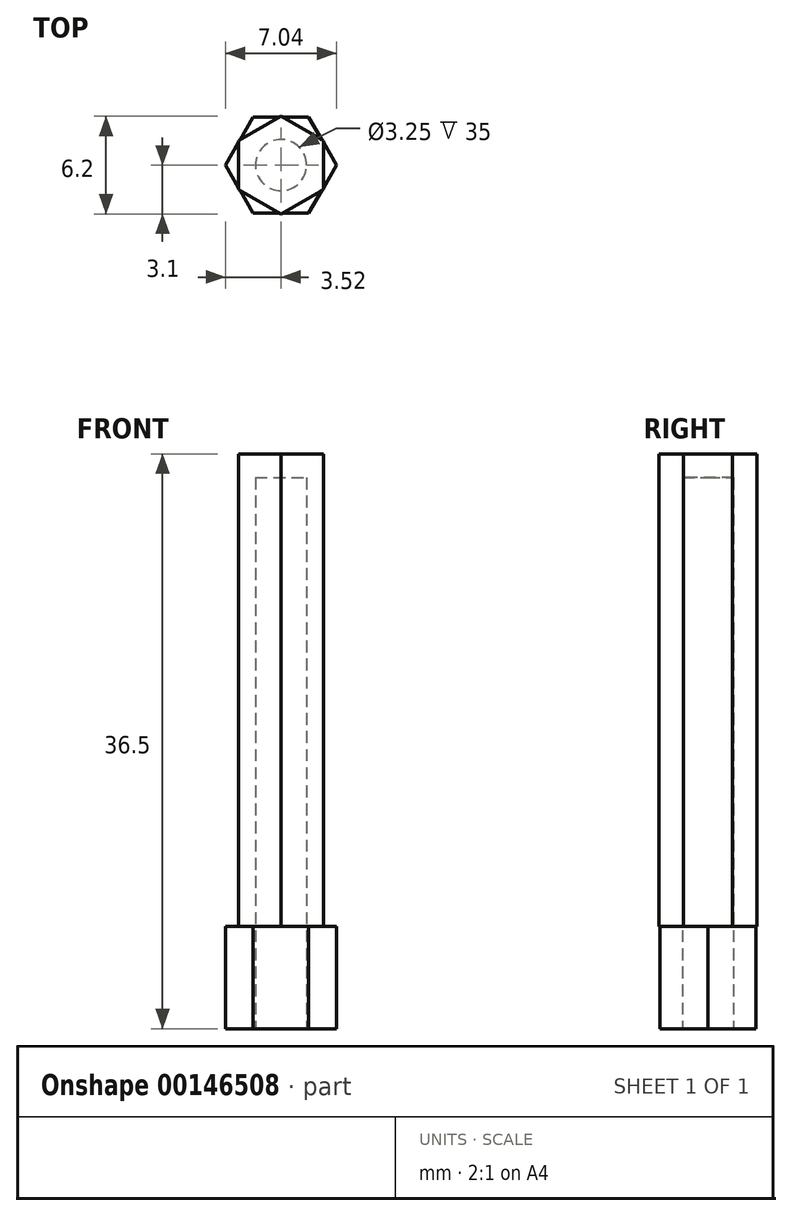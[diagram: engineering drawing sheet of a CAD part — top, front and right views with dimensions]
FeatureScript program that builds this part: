
annotation { "Feature Type Name" : "Feature", "Feature Type Description" : "" }
export const myFeature = defineFeature(function(context is Context, id is Id, definition is map)
    precondition{}
    {
        {
            var Q0;
            Q0=qCreatedBy(makeId("Top.planeOp"),FACE);
            var sketch = newSketch(context, id + "F0", { "sketchPlane" : qUnion([Q0])});
            skLineSegment(sketch, "E0", {"start": v(-1.76, -3.05) * mm, "end": v(1.76, -3.05) * mm});
            skLineSegment(sketch, "E1", {"start": v(1.76, -3.05) * mm, "end": v(3.52, 0) * mm});
            skLineSegment(sketch, "E2", {"start": v(3.52, 0) * mm, "end": v(1.76, 3.05) * mm});
            skLineSegment(sketch, "E3", {"start": v(1.76, 3.05) * mm, "end": v(-1.76, 3.05) * mm});
            skLineSegment(sketch, "E4", {"start": v(-1.76, 3.05) * mm, "end": v(-3.52, 0) * mm});
            skLineSegment(sketch, "E5", {"start": v(-3.52, 0) * mm, "end": v(-1.76, -3.05) * mm});
            skLineSegment(sketch, "E6", {"start": v(1.76, 3.05) * mm, "end": v(-1.76, -3.05) * mm, "construction": true});
            skSolve(sketch);
        }
        {
            var Q0;
            Q0 = qSketchRegion(id + "F0", true);
            extrude(context, id + "F1", {"entities" : qUnion([Q0]), "depth" : 6.5 * mm});
        }
        {
            var Q0;
            Q0=makeQuery(id+"F1.opExtrude","CAP_FACE",FACE,{"disambiguationData":[OSD([sQuery(id+"F0.wireOp",EDGE,"E0"),sQuery(id+"F0.wireOp",EDGE,"E1"),sQuery(id+"F0.wireOp",EDGE,"E2"),sQuery(id+"F0.wireOp",EDGE,"E3"),sQuery(id+"F0.wireOp",EDGE,"E4"),sQuery(id+"F0.wireOp",EDGE,"E5")])],"isStart":false});
            var sketch = newSketch(context, id + "F2", { "sketchPlane" : qUnion([Q0])});
            skLineSegment(sketch, "E7", {"start": v(0, 3.1) * mm, "end": v(-2.68, 1.55) * mm});
            skLineSegment(sketch, "E8", {"start": v(-2.68, 1.55) * mm, "end": v(-2.68, -1.55) * mm});
            skLineSegment(sketch, "E9", {"start": v(-2.68, -1.55) * mm, "end": v(0, -3.1) * mm});
            skLineSegment(sketch, "E10", {"start": v(0, -3.1) * mm, "end": v(2.68, -1.55) * mm});
            skLineSegment(sketch, "E11", {"start": v(2.68, -1.55) * mm, "end": v(2.68, 1.55) * mm});
            skLineSegment(sketch, "E12", {"start": v(2.68, 1.55) * mm, "end": v(0, 3.1) * mm});
            skLineSegment(sketch, "E13", {"start": v(0, 3.1) * mm, "end": v(0, -3.1) * mm, "construction": true});
            skSolve(sketch);
        }
        {
            var Q0;
            Q0 = qSketchRegion(id + "F2", true);
            extrude(context, id + "F3", {"entities" : qUnion([Q0]), "operationType" : NewBodyOperationType.ADD, "depth" : 30 * mm});
        }
        {
            var Q0;
            Q0=makeQuery(id+"F1.opExtrude","CAP_FACE",FACE,{"disambiguationData":[OSD([sQuery(id+"F0.wireOp",EDGE,"E0"),sQuery(id+"F0.wireOp",EDGE,"E1"),sQuery(id+"F0.wireOp",EDGE,"E2"),sQuery(id+"F0.wireOp",EDGE,"E3"),sQuery(id+"F0.wireOp",EDGE,"E4"),sQuery(id+"F0.wireOp",EDGE,"E5")])],"isStart":true});
            var sketch = newSketch(context, id + "F4", { "sketchPlane" : qUnion([Q0])});
            skCircle(sketch, "E14", {"center": v(0, 0) * mm, "radius": 1.63 * mm});
            skSolve(sketch);
        }
        {
            var Q0;
            Q0 = qSketchRegion(id + "F4", true);
            extrude(context, id + "F5", {"entities" : qUnion([Q0]), "operationType" : NewBodyOperationType.REMOVE, "oppositeDirection" : true, "depth" : 35 * mm});
        }
    });
